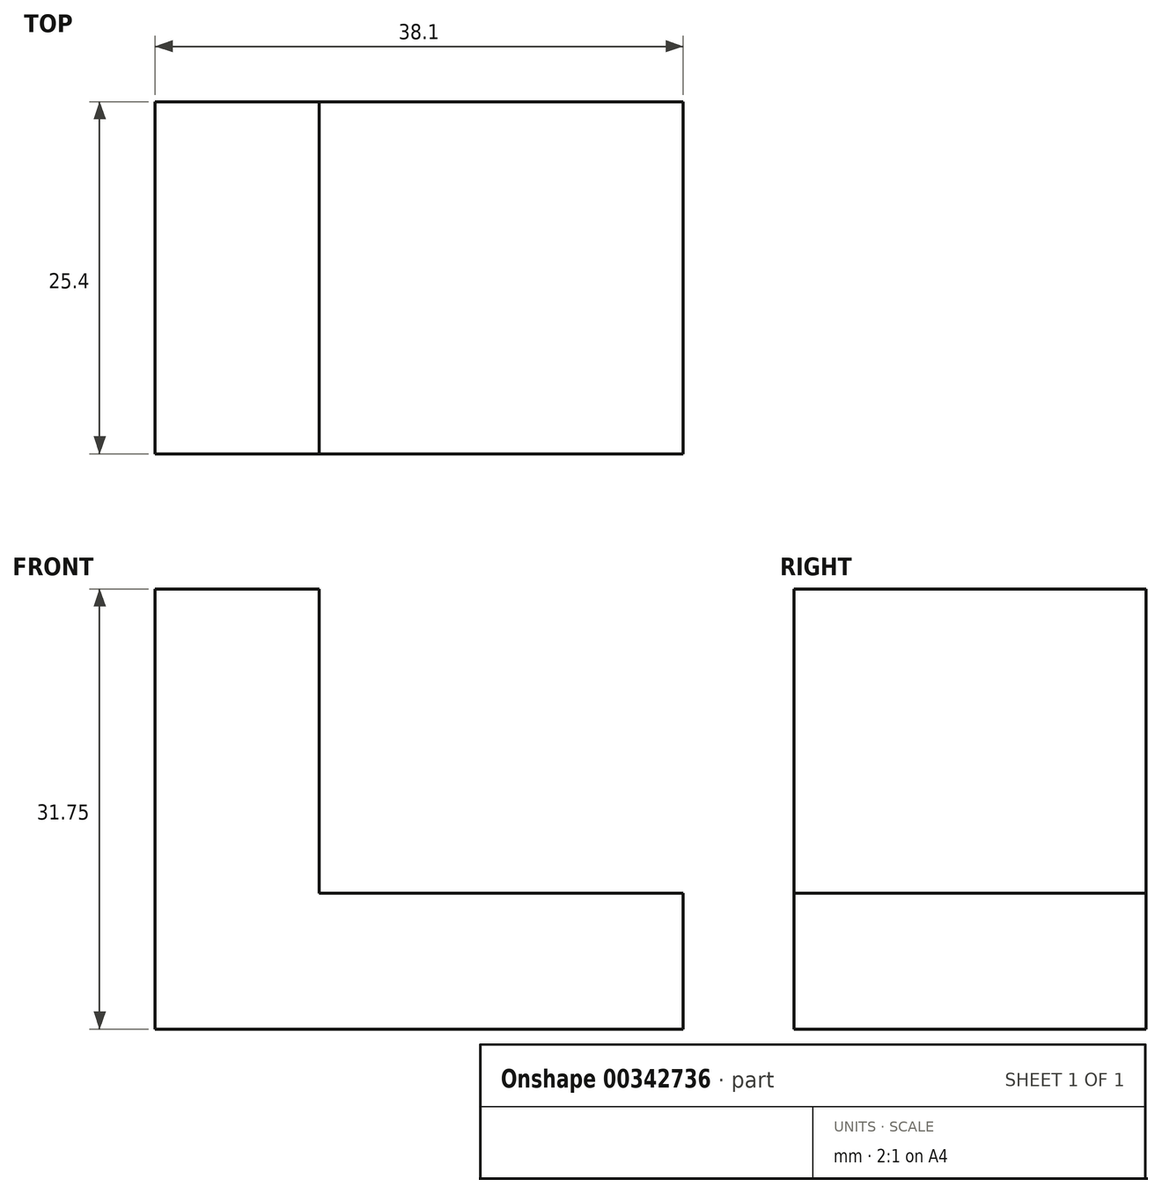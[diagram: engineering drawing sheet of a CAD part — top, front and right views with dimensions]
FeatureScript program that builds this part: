
annotation { "Feature Type Name" : "Feature", "Feature Type Description" : "" }
export const myFeature = defineFeature(function(context is Context, id is Id, definition is map)
    precondition{}
    {
        {
            var Q0;
            Q0=qCreatedBy(makeId("Front.planeOp"),FACE);
            var sketch = newSketch(context, id + "F0", { "sketchPlane" : qUnion([Q0])});
            skLineSegment(sketch, "E0", {"start": v(0, 0) * mm, "end": v(0, 31.75) * mm});
            skLineSegment(sketch, "E1", {"start": v(0, 31.75) * mm, "end": v(11.83, 31.75) * mm});
            skLineSegment(sketch, "E2", {"start": v(11.83, 31.75) * mm, "end": v(11.83, 9.81) * mm});
            skLineSegment(sketch, "E3", {"start": v(11.83, 9.81) * mm, "end": v(38.1, 9.81) * mm});
            skLineSegment(sketch, "E4", {"start": v(38.1, 9.81) * mm, "end": v(38.1, 0) * mm});
            skLineSegment(sketch, "E5", {"start": v(38.1, 0) * mm, "end": v(0, 0) * mm});
            skSolve(sketch);
        }
        {
            var Q0;
            Q0=makeQuery(id+"F0.imprint","IMPRINT",FACE,{"disambiguationData":[TD([[makeQuery(id+"F0.imprint","IMPRINT",EDGE,{"derivedFrom":sQuery(id+"F0.wireOp",EDGE,"E0")}),-1.0]])]});
            extrude(context, id + "F1", {"entities" : qUnion([Q0]), "depth" : 25.4 * mm});
        }
    });
